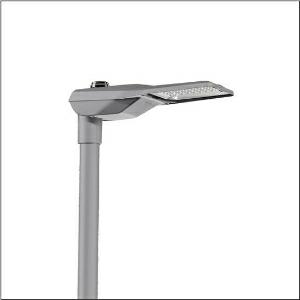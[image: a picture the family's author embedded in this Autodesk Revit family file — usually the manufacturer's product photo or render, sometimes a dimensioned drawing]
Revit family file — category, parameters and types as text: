
# Revit family: streetlight_sl_21_mini___p1_0a_5xe6a47n08hb_abf4
name_source: partatom
category: Lighting Fixtures
units: mm (PartAtom-declared; Revit-internal decimal feet)

## family parameters
Cut with Voids When Loaded = No
Host = Face
Light Source = No
Part Type = Normal
Room Calculation Point = No
Round Connector Dimension = Use Diameter
Shared = No

## types (1)
- --- (1 x LED, 9430 lm, 66 W, 4000K)
    Apparent Load = 66 VA
    CIE Flux Codes = 21 50 90 100 100
    Color Rendering = 70
    Color Temperature = 4000K
    Default Elevation = 1800 mm
    Description = Streetlight SL 21 mini, mast luminaire, primary light control with lens, of PMMA, primary optical cover: cover, of toughened safety glass, transparent, light distribution: P1.0a, light emission: direct distribution, primary light characteristic: asymmetric, installation type: side-entry, LED, 3G 1.5mm², High Power LED, rated luminous flux: 9.430lm, luminous efficacy: 143lm/W, light colour: 740, colour temperature: 4000K, control gear: NEMA (7pin), control: overheat protection, pre-setting: linear dimming characteristic, constant luminous flux control, time-dependent luminous flux control, flexible luminous flux parameterisation, mains connection: 230..240V, AC, 50/60Hz, connection cable pre-assembled, cable length: 8,5m, wiring characteristics: H07RN-F, start of lifetime: 66W, end of service life: 69W, reduction: 30W, luminaire housing, of diecast aluminium (EN AC-44300), powder-coated, SITECO metallic grey (DB 702S), corrosivity category C5 high according to DIN EN ISO 12944, multi-level sealing system, sealing non-destructively replaceable, inclination adjustable: 0°, 5°, 10°, 15°, length: 628mm, width: 235mm, height: 110mm, spigot size: 42mm (side-entry), mounting height: 4..8m, protection rating (complete): IP66, insulation class (complete): insulation class I (protective earthing), certification: CE, ENEC, ENEC+, VDE, impact resistance: IK10, permissible operating ambient temperature for outdoor applications: -40..+50°C, standard-compliant lighting for roads and squares, packaging unit: 1 piece

Light Distribution: P1.0a
    Height = 110 mm
    Lamp = 1 x LED
    Lamp Light Flux = 9430 lm
    Lamp Power = 66 W
    Lamp count = 1
    Length = 625 mm
    Luminous efficacy = 143 lm/W
    Manufacturer = Siteco
    ModVariant = No
    Model = 5XE6A47N08HB
    Number of Poles = 1
    OnlyDefault = Yes
    Power Factor = 1
    Product Name = Streetlight SL 21 mini | P1.0a
    Product group = mast luminaire | pylon top
    ProductGroupID = 6100
    Protection Class = Protection class I
    Protection Degree = IP 66
    RLX_Detail_Level = 1
    RLX_Emergency_Light_Flux = 0 lm
    RLX_Emergency_Type = 0
    RLX_Emergency_Type_DB = No
    RlxData = <blob elided: 37369 chars, md5=17a192f1>
    Socket = socket
    Standby Power = 0 W
    System Light Flux = 9430 lm
    System Power = 66 W
    Type Comments = factory setting: luminous flux: 100 % | dim-lin: 254 | 670 mA
    Type Image = l_1294379.jpg
    URL = http://relux.com
    VarID = @adj_134095
    Voltage = 0 V
    Weight = 0.00 kg
    Width = 234 mm

## geometry (parser evidence)
native form markers: Blend x4, Sweep x10
no freeform markers — native parametric forms only
